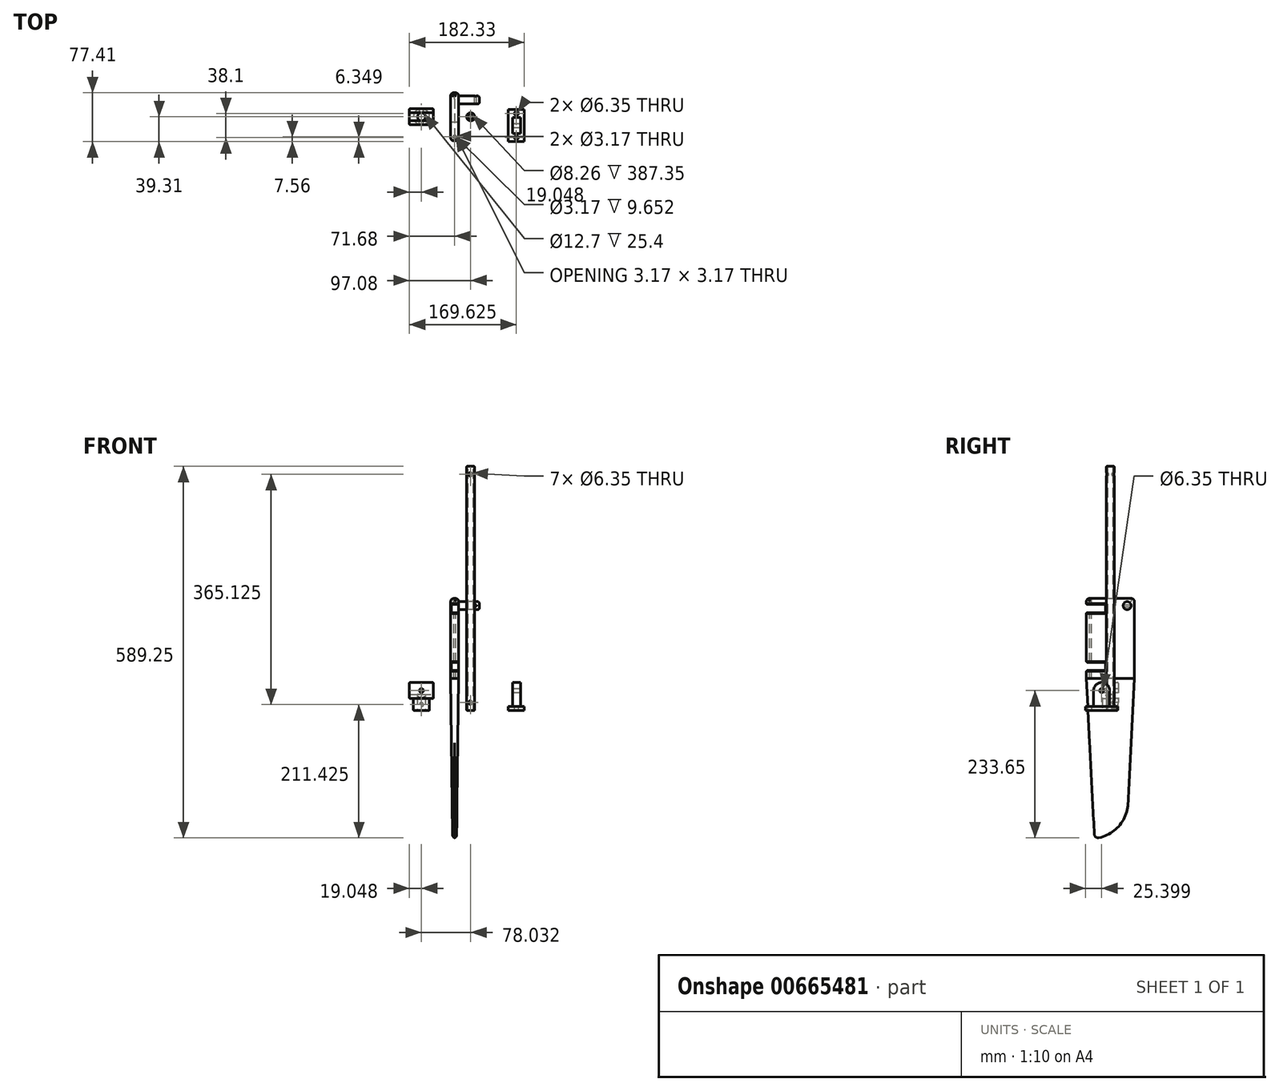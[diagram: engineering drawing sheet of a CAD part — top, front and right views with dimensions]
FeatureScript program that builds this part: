
annotation { "Feature Type Name" : "Feature", "Feature Type Description" : "" }
export const myFeature = defineFeature(function(context is Context, id is Id, definition is map)
    precondition{}
    {
        {
            var Q0;
            Q0=qCreatedBy(makeId("Right.planeOp"),FACE);
            var sketch = newSketch(context, id + "F0", { "sketchPlane" : qUnion([Q0])});
            skLineSegment(sketch, "E0", {"start": v(-41.4, 49.75) * mm, "end": v(34.8, 49.75) * mm});
            skLineSegment(sketch, "E1", {"start": v(34.8, 49.75) * mm, "end": v(34.8, -205.02) * mm});
            skArc(sketch, "E2", {"start": v(-20.7, -187.52) * mm, "mid": v(-12.8, -199.16) * mm, "end": v(0, -205.02) * mm});
            skLineSegment(sketch, "E3", {"start": v(-41.4, 49.75) * mm, "end": v(-20.7, -187.52) * mm});
            skLineSegment(sketch, "E4", {"start": v(0, -205.02) * mm, "end": v(34.8, -205.02) * mm});
            skSolve(sketch);
        }
        {
            var Q0;
            Q0=qCreatedBy(makeId("Top.planeOp"),FACE);
            cPlane(context, id + "F1", {"entities" : qUnion([Q0]), "cplaneType" : CPlaneType.OFFSET, "offset" : 50.8 * mm, "width" : 152.4 * mm, "height" : 152.4 * mm});
        }
        {
            var Q0;
            Q0=qCreatedBy(makeId("Top.planeOp"),FACE);
            cPlane(context, id + "F2", {"entities" : qUnion([Q0]), "cplaneType" : CPlaneType.OFFSET, "offset" : 203.2 * mm, "oppositeDirection" : true, "width" : 152.4 * mm, "height" : 152.4 * mm});
        }
        {
            var Q0;
            Q0=qCreatedBy(id+"F2.planeOp",FACE);
            var sketch = newSketch(context, id + "F3", { "sketchPlane" : qUnion([Q0])});
            skLineSegment(sketch, "E5.bottom", {"start": v(-3.18, 25.4) * mm, "end": v(3.17, 25.4) * mm});
            skLineSegment(sketch, "E5.top", {"start": v(-3.17, -25.4) * mm, "end": v(3.18, -25.4) * mm});
            skLineSegment(sketch, "E5.left", {"start": v(-3.18, 25.4) * mm, "end": v(-3.17, -25.4) * mm});
            skLineSegment(sketch, "E5.right", {"start": v(3.17, 25.4) * mm, "end": v(3.18, -25.4) * mm});
            skPoint(sketch, "E5.middle", {"position": v(0, 0) * mm});
            skSolve(sketch);
        }
        {
            var Q0;
            Q0=qCreatedBy(id+"F1.planeOp",FACE);
            var sketch = newSketch(context, id + "F4", { "sketchPlane" : qUnion([Q0])});
            skLineSegment(sketch, "E6.bottom", {"start": v(-6.35, 38.1) * mm, "end": v(6.35, 38.1) * mm});
            skLineSegment(sketch, "E6.top", {"start": v(-6.35, -38.1) * mm, "end": v(6.35, -38.1) * mm});
            skLineSegment(sketch, "E6.left", {"start": v(-6.35, 38.1) * mm, "end": v(-6.35, -38.1) * mm});
            skLineSegment(sketch, "E6.right", {"start": v(6.35, 38.1) * mm, "end": v(6.35, -38.1) * mm});
            skPoint(sketch, "E6.middle", {"position": v(0, 0) * mm});
            skSolve(sketch);
        }
        {
            var Q0;
            Q0=makeQuery(id+"F3.imprint","IMPRINT",FACE,{"disambiguationData":[TD([[makeQuery(id+"F3.imprint","IMPRINT",EDGE,{"derivedFrom":sQuery(id+"F3.wireOp",EDGE,"E5.bottom")}),-1.0]])]});
            var Q1;
            Q1=makeQuery(id+"F4.imprint","IMPRINT",FACE,{"disambiguationData":[TD([[makeQuery(id+"F4.imprint","IMPRINT",EDGE,{"derivedFrom":sQuery(id+"F4.wireOp",EDGE,"E6.bottom")}),-1.0]])]});
            loft(context, id + "F5", {"sheetProfilesArray" : [{ "sheetProfileEntities" : qUnion([Q0]) }, { "sheetProfileEntities" : qUnion([Q1]) }]});
        }
        {
            var Q0;
            Q0=makeQuery(id+"F5.opLoft","MID_CAP_EDGE",EDGE,{"disambiguationData":[OSD([sQuery(id+"F3.wireOp",EDGE,"E5.bottom"),sQuery(id+"F3.wireOp",EDGE,"E5.left"),sQuery(id+"F3.wireOp",EDGE,"E5.right")])],"capPos":0.0});
            fillet(context, id + "F6", {"entities" : qUnion([Q0]), "radius" : 58.8 * mm, "tangentPropagation" : true, "allowEdgeOverflow" : false});
        }
        {
            var Q0;
            {var subQ0=sQuery(id+"F3.wireOp",EDGE,"E5.right");var subQ1=sQuery(id+"F3.wireOp",EDGE,"E5.left");Q0=makeQuery(id+"F6.opFillet","BLEND_EDGE",EDGE,{"blendedFrom":[makeQuery(id+"F5.opLoft","MID_CAP_EDGE",EDGE,{"disambiguationData":[OSD([sQuery(id+"F3.wireOp",EDGE,"E5.bottom"),subQ1,subQ0])],"capPos":0.0}),makeQuery(id+"F5.opLoft","SWEPT_FACE",FACE,{"disambiguationData":[OSD([sQuery(id+"F3.wireOp",EDGE,"E5.top"),subQ1,subQ0,sQuery(id+"F4.wireOp",EDGE,"E6.top"),sQuery(id+"F4.wireOp",EDGE,"E6.left"),sQuery(id+"F4.wireOp",EDGE,"E6.right")])]})],"blendedInto":[makeQuery(id+"F5.opLoft","SWEPT_FACE",FACE,{"disambiguationData":[OSD([sQuery(id+"F3.wireOp",EDGE,"E5.top"),subQ1,subQ0,sQuery(id+"F4.wireOp",EDGE,"E6.top"),sQuery(id+"F4.wireOp",EDGE,"E6.left"),sQuery(id+"F4.wireOp",EDGE,"E6.right")])]})]});}
            fillet(context, id + "F7", {"entities" : qUnion([Q0]), "radius" : 6.33 * mm, "tangentPropagation" : true, "allowEdgeOverflow" : false});
        }
        {
            var Q0;
            {var subQ0=sQuery(id+"F3.wireOp",EDGE,"E5.right");var subQ1=sQuery(id+"F3.wireOp",EDGE,"E5.bottom");Q0=makeQuery(id+"F6.opFillet","BLEND_EDGE",EDGE,{"blendedFrom":[makeQuery(id+"F5.opLoft","MID_CAP_EDGE",EDGE,{"disambiguationData":[OSD([subQ1,sQuery(id+"F3.wireOp",EDGE,"E5.left"),subQ0])],"capPos":0.0}),makeQuery(id+"F5.opLoft","SWEPT_FACE",FACE,{"disambiguationData":[OSD([subQ1,sQuery(id+"F3.wireOp",EDGE,"E5.top"),subQ0,sQuery(id+"F4.wireOp",EDGE,"E6.bottom"),sQuery(id+"F4.wireOp",EDGE,"E6.top"),sQuery(id+"F4.wireOp",EDGE,"E6.right")])]})],"blendedInto":[makeQuery(id+"F5.opLoft","SWEPT_FACE",FACE,{"disambiguationData":[OSD([subQ1,sQuery(id+"F3.wireOp",EDGE,"E5.top"),subQ0,sQuery(id+"F4.wireOp",EDGE,"E6.bottom"),sQuery(id+"F4.wireOp",EDGE,"E6.top"),sQuery(id+"F4.wireOp",EDGE,"E6.right")])]})]});}
            var Q1;
            {var subQ0=sQuery(id+"F3.wireOp",EDGE,"E5.left");var subQ1=sQuery(id+"F3.wireOp",EDGE,"E5.bottom");Q1=makeQuery(id+"F6.opFillet","BLEND_EDGE",EDGE,{"blendedFrom":[makeQuery(id+"F5.opLoft","MID_CAP_EDGE",EDGE,{"disambiguationData":[OSD([subQ1,subQ0,sQuery(id+"F3.wireOp",EDGE,"E5.right")])],"capPos":0.0}),makeQuery(id+"F5.opLoft","SWEPT_FACE",FACE,{"disambiguationData":[OSD([subQ1,sQuery(id+"F3.wireOp",EDGE,"E5.top"),subQ0,sQuery(id+"F4.wireOp",EDGE,"E6.bottom"),sQuery(id+"F4.wireOp",EDGE,"E6.top"),sQuery(id+"F4.wireOp",EDGE,"E6.left")])]})],"blendedInto":[makeQuery(id+"F5.opLoft","SWEPT_FACE",FACE,{"disambiguationData":[OSD([subQ1,sQuery(id+"F3.wireOp",EDGE,"E5.top"),subQ0,sQuery(id+"F4.wireOp",EDGE,"E6.bottom"),sQuery(id+"F4.wireOp",EDGE,"E6.top"),sQuery(id+"F4.wireOp",EDGE,"E6.left")])]})]});}
            fillet(context, id + "F8", {"entities" : qUnion([Q0, Q1]), "radius" : 5.08 * mm, "tangentPropagation" : true, "allowEdgeOverflow" : false});
        }
        {
            var Q0;
            Q0=makeQuery(id+"F5.opLoft","CAP_FACE",FACE,{"disambiguationData":[OSD([makeQuery(id+"F4.imprint","IMPRINT",FACE,{"disambiguationData":[TD([[makeQuery(id+"F4.imprint","IMPRINT",EDGE,{"derivedFrom":sQuery(id+"F4.wireOp",EDGE,"E6.bottom")}),-1.0]])]})])],"isStart":true});
            extrude(context, id + "F9", {"entities" : qUnion([Q0]), "depth" : 127 * mm, "offsetDistance" : 25.4 * mm});
        }
        {
            var Q0;
            Q0=makeQuery(id+"F9.opExtrude","SWEPT_FACE",FACE,{"disambiguationData":[OSD([sQuery(id+"F4.wireOp",EDGE,"E6.bottom"),sQuery(id+"F4.wireOp",EDGE,"E6.top"),sQuery(id+"F4.wireOp",EDGE,"E6.right")])]});
            var sketch = newSketch(context, id + "F10", { "sketchPlane" : qUnion([Q0])});
            skLineSegment(sketch, "E7.bottom", {"start": v(-58.18, 168.15) * mm, "end": v(-7.85, 168.15) * mm});
            skLineSegment(sketch, "E7.top", {"start": v(-58.18, 155.2) * mm, "end": v(-7.85, 155.2) * mm});
            skLineSegment(sketch, "E7.left", {"start": v(-58.18, 168.15) * mm, "end": v(-58.18, 155.2) * mm});
            skLineSegment(sketch, "E7.right", {"start": v(-7.85, 168.15) * mm, "end": v(-7.85, 155.2) * mm});
            skPoint(sketch, "E7.middle", {"position": v(-33.02, 161.67) * mm});
            skLineSegment(sketch, "E8.bottom", {"start": v(-58.18, 76.45) * mm, "end": v(-7.85, 76.45) * mm});
            skLineSegment(sketch, "E8.top", {"start": v(-58.18, 63.5) * mm, "end": v(-7.85, 63.5) * mm});
            skLineSegment(sketch, "E8.left", {"start": v(-58.18, 76.45) * mm, "end": v(-58.18, 63.5) * mm});
            skLineSegment(sketch, "E8.right", {"start": v(-7.85, 76.45) * mm, "end": v(-7.85, 63.5) * mm});
            skPoint(sketch, "E8.middle", {"position": v(-33.02, 69.98) * mm});
            skSolve(sketch);
        }
        {
            var Q0;
            {var subQ0=sQuery(id+"F10.wireOp",EDGE,"E7.right");Q0=makeQuery(id+"F10.imprint","IMPRINT",FACE,{"disambiguationData":[TD([[makeQuery(id+"F10.imprint","IMPRINT",EDGE,{"derivedFrom":subQ0}),-1.0]])]});}
            var Q1;
            {var subQ0=sQuery(id+"F10.wireOp",EDGE,"E7.left");Q1=makeQuery(id+"F10.imprint","IMPRINT",FACE,{"disambiguationData":[TD([[makeQuery(id+"F10.imprint","IMPRINT",EDGE,{"derivedFrom":subQ0}),1.0]])]});}
            var Q2;
            {var subQ0=sQuery(id+"F10.wireOp",EDGE,"E8.right");Q2=makeQuery(id+"F10.imprint","IMPRINT",FACE,{"disambiguationData":[TD([[makeQuery(id+"F10.imprint","IMPRINT",EDGE,{"derivedFrom":subQ0}),-1.0]])]});}
            var Q3;
            {var subQ0=sQuery(id+"F10.wireOp",EDGE,"E8.left");Q3=makeQuery(id+"F10.imprint","IMPRINT",FACE,{"disambiguationData":[TD([[makeQuery(id+"F10.imprint","IMPRINT",EDGE,{"derivedFrom":subQ0}),1.0]])]});}
            extrude(context, id + "F11", {"entities" : qUnion([Q0, Q1, Q2, Q3]), "operationType" : NewBodyOperationType.REMOVE, "oppositeDirection" : true, "depth" : 25.4 * mm, "offsetDistance" : 25.4 * mm});
        }
        {
            var Q0;
            Q0=makeQuery(id+"F11.boolean.opBoolean","COPY",EDGE,{"derivedFrom":makeQuery(id+"F11.opExtrude","CAP_EDGE",EDGE,{"disambiguationData":[OSD([sQuery(id+"F10.wireOp",EDGE,"E7.bottom")])],"isStart":true})});
            var Q1;
            Q1=makeQuery(id+"F11.boolean.opBoolean","INTERSECT",EDGE,{"derivedFrom":[makeQuery(id+"F9.opExtrude","SWEPT_FACE",FACE,{"disambiguationData":[OSD([sQuery(id+"F4.wireOp",EDGE,"E6.bottom"),sQuery(id+"F4.wireOp",EDGE,"E6.top"),sQuery(id+"F4.wireOp",EDGE,"E6.left")])]}),makeQuery(id+"F11.opExtrude","SWEPT_FACE",FACE,{"disambiguationData":[OSD([sQuery(id+"F10.wireOp",EDGE,"E7.top")])]})]});
            var Q2;
            {var subQ0=sQuery(id+"F4.wireOp",EDGE,"E6.top");var subQ1=sQuery(id+"F4.wireOp",EDGE,"E6.left");Q2=makeQuery(id+"F11.boolean.opBoolean","INTERSECT",EDGE,{"derivedFrom":[makeQuery(id+"F9.opExtrude","SWEPT_FACE",FACE,{"disambiguationData":[OSD([sQuery(id+"F3.wireOp",EDGE,"E5.top"),sQuery(id+"F3.wireOp",EDGE,"E5.left"),subQ0,subQ1,makeQuery(id+"F4.imprint","IMPRINT",FACE,{"disambiguationData":[TD([[makeQuery(id+"F4.imprint","IMPRINT",EDGE,{"derivedFrom":sQuery(id+"F4.wireOp",EDGE,"E6.bottom")}),-1.0]])]})])]}),makeQuery(id+"F11.opExtrude","SWEPT_FACE",FACE,{"disambiguationData":[OSD([sQuery(id+"F10.wireOp",EDGE,"E7.top")])]})]});}
            var Q3;
            {var subQ0=sQuery(id+"F4.wireOp",EDGE,"E6.top");var subQ1=sQuery(id+"F4.wireOp",EDGE,"E6.right");Q3=makeQuery(id+"F11.boolean.opBoolean","INTERSECT",EDGE,{"derivedFrom":[makeQuery(id+"F9.opExtrude","SWEPT_FACE",FACE,{"disambiguationData":[OSD([sQuery(id+"F3.wireOp",EDGE,"E5.top"),sQuery(id+"F3.wireOp",EDGE,"E5.right"),subQ0,subQ1,makeQuery(id+"F4.imprint","IMPRINT",FACE,{"disambiguationData":[TD([[makeQuery(id+"F4.imprint","IMPRINT",EDGE,{"derivedFrom":sQuery(id+"F4.wireOp",EDGE,"E6.bottom")}),-1.0]])]})])]}),makeQuery(id+"F11.opExtrude","SWEPT_FACE",FACE,{"disambiguationData":[OSD([sQuery(id+"F10.wireOp",EDGE,"E7.top")])]})]});}
            var Q4;
            Q4=makeQuery(id+"F11.boolean.opBoolean","COPY",EDGE,{"derivedFrom":makeQuery(id+"F11.opExtrude","CAP_EDGE",EDGE,{"disambiguationData":[OSD([sQuery(id+"F10.wireOp",EDGE,"E7.top")])],"isStart":true})});
            var Q5;
            Q5=makeQuery(id+"F11.boolean.opBoolean","INTERSECT",EDGE,{"derivedFrom":[makeQuery(id+"F9.opExtrude","SWEPT_FACE",FACE,{"disambiguationData":[OSD([sQuery(id+"F4.wireOp",EDGE,"E6.top"),sQuery(id+"F4.wireOp",EDGE,"E6.left"),sQuery(id+"F4.wireOp",EDGE,"E6.right")])]}),makeQuery(id+"F11.opExtrude","SWEPT_FACE",FACE,{"disambiguationData":[OSD([sQuery(id+"F10.wireOp",EDGE,"E7.top")])]})]});
            var Q6;
            {var subQ0=sQuery(id+"F4.wireOp",EDGE,"E6.top");var subQ1=sQuery(id+"F4.wireOp",EDGE,"E6.right");Q6=makeQuery(id+"F11.boolean.opBoolean","INTERSECT",EDGE,{"derivedFrom":[makeQuery(id+"F9.opExtrude","SWEPT_FACE",FACE,{"disambiguationData":[OSD([sQuery(id+"F3.wireOp",EDGE,"E5.top"),sQuery(id+"F3.wireOp",EDGE,"E5.right"),subQ0,subQ1,makeQuery(id+"F4.imprint","IMPRINT",FACE,{"disambiguationData":[TD([[makeQuery(id+"F4.imprint","IMPRINT",EDGE,{"derivedFrom":sQuery(id+"F4.wireOp",EDGE,"E6.bottom")}),-1.0]])]})])]}),makeQuery(id+"F11.opExtrude","SWEPT_FACE",FACE,{"disambiguationData":[OSD([sQuery(id+"F10.wireOp",EDGE,"E7.bottom")])]})]});}
            var Q7;
            Q7=makeQuery(id+"F11.boolean.opBoolean","INTERSECT",EDGE,{"derivedFrom":[makeQuery(id+"F9.opExtrude","SWEPT_FACE",FACE,{"disambiguationData":[OSD([sQuery(id+"F4.wireOp",EDGE,"E6.top"),sQuery(id+"F4.wireOp",EDGE,"E6.left"),sQuery(id+"F4.wireOp",EDGE,"E6.right")])]}),makeQuery(id+"F11.opExtrude","SWEPT_FACE",FACE,{"disambiguationData":[OSD([sQuery(id+"F10.wireOp",EDGE,"E7.bottom")])]})]});
            var Q8;
            {var subQ0=sQuery(id+"F4.wireOp",EDGE,"E6.top");var subQ1=sQuery(id+"F4.wireOp",EDGE,"E6.left");Q8=makeQuery(id+"F11.boolean.opBoolean","INTERSECT",EDGE,{"derivedFrom":[makeQuery(id+"F9.opExtrude","SWEPT_FACE",FACE,{"disambiguationData":[OSD([sQuery(id+"F3.wireOp",EDGE,"E5.top"),sQuery(id+"F3.wireOp",EDGE,"E5.left"),subQ0,subQ1,makeQuery(id+"F4.imprint","IMPRINT",FACE,{"disambiguationData":[TD([[makeQuery(id+"F4.imprint","IMPRINT",EDGE,{"derivedFrom":sQuery(id+"F4.wireOp",EDGE,"E6.bottom")}),-1.0]])]})])]}),makeQuery(id+"F11.opExtrude","SWEPT_FACE",FACE,{"disambiguationData":[OSD([sQuery(id+"F10.wireOp",EDGE,"E7.bottom")])]})]});}
            var Q9;
            Q9=makeQuery(id+"F11.boolean.opBoolean","INTERSECT",EDGE,{"derivedFrom":[makeQuery(id+"F9.opExtrude","SWEPT_FACE",FACE,{"disambiguationData":[OSD([sQuery(id+"F4.wireOp",EDGE,"E6.bottom"),sQuery(id+"F4.wireOp",EDGE,"E6.top"),sQuery(id+"F4.wireOp",EDGE,"E6.left")])]}),makeQuery(id+"F11.opExtrude","SWEPT_FACE",FACE,{"disambiguationData":[OSD([sQuery(id+"F10.wireOp",EDGE,"E7.bottom")])]})]});
            var Q10;
            Q10=makeQuery(id+"F11.boolean.opBoolean","INTERSECT",EDGE,{"derivedFrom":[makeQuery(id+"F9.opExtrude","SWEPT_FACE",FACE,{"disambiguationData":[OSD([sQuery(id+"F4.wireOp",EDGE,"E6.bottom"),sQuery(id+"F4.wireOp",EDGE,"E6.top"),sQuery(id+"F4.wireOp",EDGE,"E6.left")])]}),makeQuery(id+"F11.opExtrude","SWEPT_FACE",FACE,{"disambiguationData":[OSD([sQuery(id+"F10.wireOp",EDGE,"E7.right")])]})]});
            var Q11;
            Q11=makeQuery(id+"F11.boolean.opBoolean","COPY",EDGE,{"derivedFrom":makeQuery(id+"F11.opExtrude","CAP_EDGE",EDGE,{"disambiguationData":[OSD([sQuery(id+"F10.wireOp",EDGE,"E7.right")])],"isStart":true})});
            var Q12;
            Q12=makeQuery(id+"F11.boolean.opBoolean","INTERSECT",EDGE,{"derivedFrom":[makeQuery(id+"F9.opExtrude","SWEPT_FACE",FACE,{"disambiguationData":[OSD([sQuery(id+"F4.wireOp",EDGE,"E6.bottom"),sQuery(id+"F4.wireOp",EDGE,"E6.top"),sQuery(id+"F4.wireOp",EDGE,"E6.left")])]}),makeQuery(id+"F11.opExtrude","SWEPT_FACE",FACE,{"disambiguationData":[OSD([sQuery(id+"F10.wireOp",EDGE,"E8.right")])]})]});
            var Q13;
            Q13=makeQuery(id+"F11.boolean.opBoolean","INTERSECT",EDGE,{"derivedFrom":[makeQuery(id+"F9.opExtrude","SWEPT_FACE",FACE,{"disambiguationData":[OSD([sQuery(id+"F4.wireOp",EDGE,"E6.bottom"),sQuery(id+"F4.wireOp",EDGE,"E6.top"),sQuery(id+"F4.wireOp",EDGE,"E6.left")])]}),makeQuery(id+"F11.opExtrude","SWEPT_FACE",FACE,{"disambiguationData":[OSD([sQuery(id+"F10.wireOp",EDGE,"E8.top")])]})]});
            var Q14;
            Q14=makeQuery(id+"F11.boolean.opBoolean","INTERSECT",EDGE,{"derivedFrom":[makeQuery(id+"F9.opExtrude","SWEPT_FACE",FACE,{"disambiguationData":[OSD([sQuery(id+"F4.wireOp",EDGE,"E6.bottom"),sQuery(id+"F4.wireOp",EDGE,"E6.top"),sQuery(id+"F4.wireOp",EDGE,"E6.left")])]}),makeQuery(id+"F11.opExtrude","SWEPT_FACE",FACE,{"disambiguationData":[OSD([sQuery(id+"F10.wireOp",EDGE,"E8.bottom")])]})]});
            var Q15;
            Q15=makeQuery(id+"F11.boolean.opBoolean","COPY",EDGE,{"derivedFrom":makeQuery(id+"F11.opExtrude","CAP_EDGE",EDGE,{"disambiguationData":[OSD([sQuery(id+"F10.wireOp",EDGE,"E8.right")])],"isStart":true})});
            var Q16;
            Q16=makeQuery(id+"F11.boolean.opBoolean","COPY",EDGE,{"derivedFrom":makeQuery(id+"F11.opExtrude","CAP_EDGE",EDGE,{"disambiguationData":[OSD([sQuery(id+"F10.wireOp",EDGE,"E8.top")])],"isStart":true})});
            var Q17;
            {var subQ0=sQuery(id+"F4.wireOp",EDGE,"E6.top");var subQ1=sQuery(id+"F4.wireOp",EDGE,"E6.left");Q17=makeQuery(id+"F11.boolean.opBoolean","INTERSECT",EDGE,{"derivedFrom":[makeQuery(id+"F9.opExtrude","SWEPT_FACE",FACE,{"disambiguationData":[OSD([sQuery(id+"F3.wireOp",EDGE,"E5.top"),sQuery(id+"F3.wireOp",EDGE,"E5.left"),subQ0,subQ1,makeQuery(id+"F4.imprint","IMPRINT",FACE,{"disambiguationData":[TD([[makeQuery(id+"F4.imprint","IMPRINT",EDGE,{"derivedFrom":sQuery(id+"F4.wireOp",EDGE,"E6.bottom")}),-1.0]])]})])]}),makeQuery(id+"F11.opExtrude","SWEPT_FACE",FACE,{"disambiguationData":[OSD([sQuery(id+"F10.wireOp",EDGE,"E8.top")])]})]});}
            var Q18;
            {var subQ0=sQuery(id+"F4.wireOp",EDGE,"E6.top");var subQ1=sQuery(id+"F4.wireOp",EDGE,"E6.right");Q18=makeQuery(id+"F11.boolean.opBoolean","INTERSECT",EDGE,{"derivedFrom":[makeQuery(id+"F9.opExtrude","SWEPT_FACE",FACE,{"disambiguationData":[OSD([sQuery(id+"F3.wireOp",EDGE,"E5.top"),sQuery(id+"F3.wireOp",EDGE,"E5.right"),subQ0,subQ1,makeQuery(id+"F4.imprint","IMPRINT",FACE,{"disambiguationData":[TD([[makeQuery(id+"F4.imprint","IMPRINT",EDGE,{"derivedFrom":sQuery(id+"F4.wireOp",EDGE,"E6.bottom")}),-1.0]])]})])]}),makeQuery(id+"F11.opExtrude","SWEPT_FACE",FACE,{"disambiguationData":[OSD([sQuery(id+"F10.wireOp",EDGE,"E8.top")])]})]});}
            var Q19;
            Q19=makeQuery(id+"F11.boolean.opBoolean","INTERSECT",EDGE,{"derivedFrom":[makeQuery(id+"F9.opExtrude","SWEPT_FACE",FACE,{"disambiguationData":[OSD([sQuery(id+"F4.wireOp",EDGE,"E6.top"),sQuery(id+"F4.wireOp",EDGE,"E6.left"),sQuery(id+"F4.wireOp",EDGE,"E6.right")])]}),makeQuery(id+"F11.opExtrude","SWEPT_FACE",FACE,{"disambiguationData":[OSD([sQuery(id+"F10.wireOp",EDGE,"E8.top")])]})]});
            var Q20;
            {var subQ0=sQuery(id+"F4.wireOp",EDGE,"E6.top");var subQ1=sQuery(id+"F4.wireOp",EDGE,"E6.left");Q20=makeQuery(id+"F11.boolean.opBoolean","INTERSECT",EDGE,{"derivedFrom":[makeQuery(id+"F9.opExtrude","SWEPT_FACE",FACE,{"disambiguationData":[OSD([sQuery(id+"F3.wireOp",EDGE,"E5.top"),sQuery(id+"F3.wireOp",EDGE,"E5.left"),subQ0,subQ1,makeQuery(id+"F4.imprint","IMPRINT",FACE,{"disambiguationData":[TD([[makeQuery(id+"F4.imprint","IMPRINT",EDGE,{"derivedFrom":sQuery(id+"F4.wireOp",EDGE,"E6.bottom")}),-1.0]])]})])]}),makeQuery(id+"F11.opExtrude","SWEPT_FACE",FACE,{"disambiguationData":[OSD([sQuery(id+"F10.wireOp",EDGE,"E8.bottom")])]})]});}
            var Q21;
            Q21=makeQuery(id+"F11.boolean.opBoolean","INTERSECT",EDGE,{"derivedFrom":[makeQuery(id+"F9.opExtrude","SWEPT_FACE",FACE,{"disambiguationData":[OSD([sQuery(id+"F4.wireOp",EDGE,"E6.top"),sQuery(id+"F4.wireOp",EDGE,"E6.left"),sQuery(id+"F4.wireOp",EDGE,"E6.right")])]}),makeQuery(id+"F11.opExtrude","SWEPT_FACE",FACE,{"disambiguationData":[OSD([sQuery(id+"F10.wireOp",EDGE,"E8.bottom")])]})]});
            var Q22;
            {var subQ0=sQuery(id+"F4.wireOp",EDGE,"E6.top");var subQ1=sQuery(id+"F4.wireOp",EDGE,"E6.right");Q22=makeQuery(id+"F11.boolean.opBoolean","INTERSECT",EDGE,{"derivedFrom":[makeQuery(id+"F9.opExtrude","SWEPT_FACE",FACE,{"disambiguationData":[OSD([sQuery(id+"F3.wireOp",EDGE,"E5.top"),sQuery(id+"F3.wireOp",EDGE,"E5.right"),subQ0,subQ1,makeQuery(id+"F4.imprint","IMPRINT",FACE,{"disambiguationData":[TD([[makeQuery(id+"F4.imprint","IMPRINT",EDGE,{"derivedFrom":sQuery(id+"F4.wireOp",EDGE,"E6.bottom")}),-1.0]])]})])]}),makeQuery(id+"F11.opExtrude","SWEPT_FACE",FACE,{"disambiguationData":[OSD([sQuery(id+"F10.wireOp",EDGE,"E8.bottom")])]})]});}
            var Q23;
            Q23=makeQuery(id+"F11.boolean.opBoolean","COPY",EDGE,{"derivedFrom":makeQuery(id+"F11.opExtrude","CAP_EDGE",EDGE,{"disambiguationData":[OSD([sQuery(id+"F10.wireOp",EDGE,"E8.bottom")])],"isStart":true})});
            chamfer(context, id + "F12", {"entities" : qUnion([Q0, Q1, Q2, Q3, Q4, Q5, Q6, Q7, Q8, Q9, Q10, Q11, Q12, Q13, Q14, Q15, Q16, Q17, Q18, Q19, Q20, Q21, Q22, Q23]), "width" : 1.27 * mm, "tangentPropagation" : true});
        }
        {
            var Q0;
            Q0=makeQuery(id+"F9.opExtrude","CAP_FACE",FACE,{"disambiguationData":[OSD([makeQuery(id+"F4.imprint","IMPRINT",FACE,{"disambiguationData":[TD([[makeQuery(id+"F4.imprint","IMPRINT",EDGE,{"derivedFrom":sQuery(id+"F4.wireOp",EDGE,"E6.bottom")}),-1.0]])]})])],"isStart":false});
            var sketch = newSketch(context, id + "F13", { "sketchPlane" : qUnion([Q0])});
            skCircle(sketch, "E9", {"center": v(0, -31.75) * mm, "radius": 1.59 * mm});
            skSolve(sketch);
        }
        {
            var Q0;
            Q0=makeQuery(id+"F13.imprint","IMPRINT",FACE,{"disambiguationData":[TD([[makeQuery(id+"F13.imprint","IMPRINT",EDGE,{"derivedFrom":sQuery(id+"F13.wireOp",EDGE,"E9")}),1.0]])]});
            extrude(context, id + "F14", {"entities" : qUnion([Q0]), "operationType" : NewBodyOperationType.REMOVE, "oppositeDirection" : true, "depth" : 127 * mm, "offsetDistance" : 25.4 * mm});
        }
        {
            var Q0;
            Q0=makeQuery(id+"F9.opExtrude","CAP_EDGE",EDGE,{"disambiguationData":[OSD([sQuery(id+"F4.wireOp",EDGE,"E6.bottom"),sQuery(id+"F4.wireOp",EDGE,"E6.top"),sQuery(id+"F4.wireOp",EDGE,"E6.left")])],"isStart":false});
            var Q1;
            Q1=makeQuery(id+"F9.opExtrude","CAP_EDGE",EDGE,{"disambiguationData":[OSD([sQuery(id+"F4.wireOp",EDGE,"E6.bottom"),sQuery(id+"F4.wireOp",EDGE,"E6.top"),sQuery(id+"F4.wireOp",EDGE,"E6.right")])],"isStart":false});
            var Q2;
            {var subQ0=sQuery(id+"F4.wireOp",EDGE,"E6.top");var subQ1=sQuery(id+"F4.wireOp",EDGE,"E6.right");Q2=makeQuery(id+"F9.opExtrude","CAP_EDGE",EDGE,{"disambiguationData":[OSD([sQuery(id+"F3.wireOp",EDGE,"E5.top"),sQuery(id+"F3.wireOp",EDGE,"E5.right"),subQ0,subQ1,makeQuery(id+"F4.imprint","IMPRINT",FACE,{"disambiguationData":[TD([[makeQuery(id+"F4.imprint","IMPRINT",EDGE,{"derivedFrom":sQuery(id+"F4.wireOp",EDGE,"E6.bottom")}),-1.0]])]})])],"isStart":false});}
            var Q3;
            {var subQ0=sQuery(id+"F4.wireOp",EDGE,"E6.top");var subQ1=sQuery(id+"F4.wireOp",EDGE,"E6.left");Q3=makeQuery(id+"F9.opExtrude","CAP_EDGE",EDGE,{"disambiguationData":[OSD([sQuery(id+"F3.wireOp",EDGE,"E5.top"),sQuery(id+"F3.wireOp",EDGE,"E5.left"),subQ0,subQ1,makeQuery(id+"F4.imprint","IMPRINT",FACE,{"disambiguationData":[TD([[makeQuery(id+"F4.imprint","IMPRINT",EDGE,{"derivedFrom":sQuery(id+"F4.wireOp",EDGE,"E6.bottom")}),-1.0]])]})])],"isStart":false});}
            var Q4;
            Q4=makeQuery(id+"F9.opExtrude","CAP_EDGE",EDGE,{"disambiguationData":[OSD([sQuery(id+"F4.wireOp",EDGE,"E6.top"),sQuery(id+"F4.wireOp",EDGE,"E6.left"),sQuery(id+"F4.wireOp",EDGE,"E6.right")])],"isStart":false});
            var Q5;
            {var subQ0=sQuery(id+"F4.wireOp",EDGE,"E6.bottom");var subQ1=sQuery(id+"F4.wireOp",EDGE,"E6.left");Q5=makeQuery(id+"F9.opExtrude","CAP_EDGE",EDGE,{"disambiguationData":[OSD([sQuery(id+"F3.wireOp",EDGE,"E5.bottom"),sQuery(id+"F3.wireOp",EDGE,"E5.left"),subQ0,subQ1,makeQuery(id+"F4.imprint","IMPRINT",FACE,{"disambiguationData":[TD([[makeQuery(id+"F4.imprint","IMPRINT",EDGE,{"derivedFrom":subQ0}),-1.0]])]})])],"isStart":false});}
            var Q6;
            {var subQ0=sQuery(id+"F4.wireOp",EDGE,"E6.bottom");var subQ1=sQuery(id+"F4.wireOp",EDGE,"E6.right");Q6=makeQuery(id+"F9.opExtrude","CAP_EDGE",EDGE,{"disambiguationData":[OSD([sQuery(id+"F3.wireOp",EDGE,"E5.bottom"),sQuery(id+"F3.wireOp",EDGE,"E5.right"),subQ0,subQ1,makeQuery(id+"F4.imprint","IMPRINT",FACE,{"disambiguationData":[TD([[makeQuery(id+"F4.imprint","IMPRINT",EDGE,{"derivedFrom":subQ0}),-1.0]])]})])],"isStart":false});}
            var Q7;
            Q7=makeQuery(id+"F9.opExtrude","CAP_EDGE",EDGE,{"disambiguationData":[OSD([sQuery(id+"F4.wireOp",EDGE,"E6.bottom"),sQuery(id+"F4.wireOp",EDGE,"E6.left"),sQuery(id+"F4.wireOp",EDGE,"E6.right")])],"isStart":false});
            fillet(context, id + "F15", {"entities" : qUnion([Q0, Q1, Q2, Q3, Q4, Q5, Q6, Q7]), "radius" : 5.08 * mm, "tangentPropagation" : true, "allowEdgeOverflow" : false});
        }
        {
            var Q0;
            Q0=qCreatedBy(makeId("Top.planeOp"),FACE);
            var sketch = newSketch(context, id + "F16", { "sketchPlane" : qUnion([Q0])});
            skCircle(sketch, "E10", {"center": v(25.4, 0) * mm, "radius": 6.35 * mm});
            skSolve(sketch);
        }
        {
            var Q0;
            Q0 = qSketchRegion(id + "F16", true);
            extrude(context, id + "F17", {"entities" : qUnion([Q0]), "depth" : 387.35 * mm, "offsetDistance" : 25.4 * mm});
        }
        {
            var Q0;
            Q0=qCreatedBy(makeId("Top.planeOp"),FACE);
            var sketch = newSketch(context, id + "F18", { "sketchPlane" : qUnion([Q0])});
            skCircle(sketch, "E11", {"center": v(-52.63, 0) * mm, "radius": 6.35 * mm});
            skCircle(sketch, "E12", {"center": v(-52.63, 0) * mm, "radius": 12.7 * mm});
            skSolve(sketch);
        }
        {
            var Q0;
            Q0=makeQuery(id+"F18.imprint","IMPRINT",FACE,{"disambiguationData":[TD([[makeQuery(id+"F18.imprint","IMPRINT",EDGE,{"derivedFrom":sQuery(id+"F18.wireOp",EDGE,"E11")}),-1.0]])]});
            extrude(context, id + "F19", {"entities" : qUnion([Q0]), "depth" : 19.05 * mm, "offsetDistance" : 25.4 * mm});
        }
        {
            var Q0;
            Q0=makeQuery(id+"F19.opExtrude","CAP_FACE",FACE,{"disambiguationData":[OSD([sQuery(id+"F18.wireOp",EDGE,"E11"),sQuery(id+"F18.wireOp",EDGE,"E12")])],"isStart":false});
            var sketch = newSketch(context, id + "F20", { "sketchPlane" : qUnion([Q0])});
            skLineSegment(sketch, "E13.bottom", {"start": v(-33.58, -12.7) * mm, "end": v(-71.68, -12.7) * mm});
            skLineSegment(sketch, "E13.top", {"start": v(-33.58, 12.7) * mm, "end": v(-71.68, 12.7) * mm});
            skLineSegment(sketch, "E13.left", {"start": v(-33.58, -12.7) * mm, "end": v(-33.58, 12.7) * mm});
            skLineSegment(sketch, "E13.right", {"start": v(-71.68, -12.7) * mm, "end": v(-71.68, 12.7) * mm});
            skPoint(sketch, "E13.middle", {"position": v(-52.63, 0) * mm});
            skLineSegment(sketch, "E14", {"start": v(-71.68, 6.35) * mm, "end": v(-33.58, 6.35) * mm});
            skLineSegment(sketch, "E15", {"start": v(-71.68, -6.35) * mm, "end": v(-33.58, -6.35) * mm});
            skSolve(sketch);
        }
        {
            var Q0;
            {var subQ4=sQuery(id+"F20.wireOp",EDGE,"E13.top");Q0=makeQuery(id+"F20.imprint","IMPRINT",FACE,{"disambiguationData":[TD([[makeQuery(id+"F20.imprint","IMPRINT",EDGE,{"derivedFrom":subQ4}),1.0]])]});}
            var Q1;
            {var subQ1=sQuery(id+"F20.wireOp",EDGE,"E13.bottom");Q1=makeQuery(id+"F20.imprint","IMPRINT",FACE,{"disambiguationData":[TD([[makeQuery(id+"F20.imprint","IMPRINT",EDGE,{"derivedFrom":subQ1}),-1.0]])]});}
            var Q2;
            {var subQ0=sQuery(id+"F20.wireOp",EDGE,"E15");var subQ1=makeQuery(id+"F19.opExtrude","CAP_EDGE",EDGE,{"disambiguationData":[OSD([sQuery(id+"F18.wireOp",EDGE,"E12")])],"isStart":false});var subQ2=makeQuery(id+"F20.imprint","INTERSECT",VERTEX,{"disambiguationData":[OD(0.0)],"derivedFrom":[subQ1,subQ0]});Q2=makeQuery(id+"F20.imprint","IMPRINT",FACE,{"disambiguationData":[TD([[makeQuery(id+"F20.imprint","IMPRINT",EDGE,{"disambiguationData":[TD([[subQ2,-1.0]])],"derivedFrom":subQ0}),-1.0]])]});}
            var Q3;
            {var subQ0=sQuery(id+"F20.wireOp",EDGE,"E14");var subQ1=makeQuery(id+"F19.opExtrude","CAP_EDGE",EDGE,{"disambiguationData":[OSD([sQuery(id+"F18.wireOp",EDGE,"E12")])],"isStart":false});var subQ2=makeQuery(id+"F20.imprint","INTERSECT",VERTEX,{"disambiguationData":[OD(0.0)],"derivedFrom":[subQ1,subQ0]});Q3=makeQuery(id+"F20.imprint","IMPRINT",FACE,{"disambiguationData":[TD([[makeQuery(id+"F20.imprint","IMPRINT",EDGE,{"disambiguationData":[TD([[subQ2,-1.0]])],"derivedFrom":subQ0}),1.0]])]});}
            extrude(context, id + "F21", {"entities" : qUnion([Q0, Q1, Q2, Q3]), "depth" : 25.4 * mm, "offsetDistance" : 25.4 * mm});
        }
        {
            var Q0;
            {var subQ0=sQuery(id+"F20.wireOp",EDGE,"E14");var subQ1=sQuery(id+"F20.wireOp",EDGE,"E13.right");var subQ2=makeQuery(id+"F20.imprint","INTERSECT",VERTEX,{"derivedFrom":[subQ1,subQ0]});Q0=makeQuery(id+"F20.imprint","IMPRINT",FACE,{"disambiguationData":[TD([[makeQuery(id+"F20.imprint","IMPRINT",EDGE,{"disambiguationData":[TD([[subQ2,1.0]])],"derivedFrom":subQ1}),-1.0]])]});}
            var Q1;
            {var subQ0=sQuery(id+"F20.wireOp",EDGE,"E14");var subQ1=sQuery(id+"F20.wireOp",EDGE,"E13.left");var subQ2=makeQuery(id+"F20.imprint","INTERSECT",VERTEX,{"derivedFrom":[subQ1,subQ0]});Q1=makeQuery(id+"F20.imprint","IMPRINT",FACE,{"disambiguationData":[TD([[makeQuery(id+"F20.imprint","IMPRINT",EDGE,{"disambiguationData":[TD([[subQ2,1.0]])],"derivedFrom":subQ1}),1.0]])]});}
            var Q2;
            {var subQ0=sQuery(id+"F20.wireOp",EDGE,"E14");var subQ1=makeQuery(id+"F19.opExtrude","CAP_EDGE",EDGE,{"disambiguationData":[OSD([sQuery(id+"F18.wireOp",EDGE,"E12")])],"isStart":false});var subQ2=makeQuery(id+"F20.imprint","INTERSECT",VERTEX,{"disambiguationData":[OD(0.0)],"derivedFrom":[subQ1,subQ0]});Q2=makeQuery(id+"F20.imprint","IMPRINT",FACE,{"disambiguationData":[TD([[makeQuery(id+"F20.imprint","IMPRINT",EDGE,{"disambiguationData":[TD([[subQ2,-1.0]])],"derivedFrom":subQ0}),-1.0]])]});}
            var Q3;
            {var subQ0=sQuery(id+"F20.wireOp",EDGE,"E14");var subQ1=makeQuery(id+"F19.opExtrude","CAP_EDGE",EDGE,{"disambiguationData":[OSD([sQuery(id+"F18.wireOp",EDGE,"E11")])],"isStart":false});var subQ2=makeQuery(id+"F20.imprint","INTERSECT",VERTEX,{"derivedFrom":[subQ1,subQ0]});Q3=makeQuery(id+"F20.imprint","IMPRINT",FACE,{"disambiguationData":[TD([[makeQuery(id+"F20.imprint","IMPRINT",EDGE,{"disambiguationData":[TD([[subQ2,-1.0]])],"derivedFrom":subQ0}),-1.0]])]});}
            extrude(context, id + "F22", {"entities" : qUnion([Q0, Q1, Q2, Q3]), "depth" : 6.35 * mm, "offsetDistance" : 25.4 * mm});
        }
        {
            var Q0;
            Q0=makeQuery(id+"F20.imprint","IMPRINT",FACE,{"disambiguationData":[TD([[makeQuery(id+"F20.imprint","IMPRINT",EDGE,{"derivedFrom":makeQuery(id+"F19.opExtrude","CAP_EDGE",EDGE,{"disambiguationData":[OSD([sQuery(id+"F18.wireOp",EDGE,"E11")])],"isStart":false})}),-1.0]])]});
            extrude(context, id + "F23", {"entities" : qUnion([Q0]), "depth" : 6.35 * mm, "offsetDistance" : 25.4 * mm});
        }
        {
            var Q0;
            Q0=makeQuery(id+"F19.opExtrude","SWEPT_BODY",BODY,{"disambiguationData":[OSD([sQuery(id+"F18.wireOp",EDGE,"E11"),sQuery(id+"F18.wireOp",EDGE,"E12")])]});
            var Q1;
            Q1=makeQuery(id+"F21.opExtrude","SWEPT_BODY",BODY,{"disambiguationData":[OSD([sQuery(id+"F20.wireOp",EDGE,"E13.bottom"),sQuery(id+"F20.wireOp",EDGE,"E13.left"),sQuery(id+"F20.wireOp",EDGE,"E13.right"),sQuery(id+"F20.wireOp",EDGE,"E15")])]});
            var Q2;
            Q2=makeQuery(id+"F21.opExtrude","SWEPT_BODY",BODY,{"disambiguationData":[OSD([sQuery(id+"F20.wireOp",EDGE,"E13.top"),sQuery(id+"F20.wireOp",EDGE,"E13.left"),sQuery(id+"F20.wireOp",EDGE,"E13.right"),sQuery(id+"F20.wireOp",EDGE,"E14")])]});
            var Q3;
            Q3=makeQuery(id+"F22.opExtrude","SWEPT_BODY",BODY,{"disambiguationData":[OSD([sQuery(id+"F18.wireOp",EDGE,"E12"),sQuery(id+"F20.wireOp",EDGE,"E13.left"),sQuery(id+"F20.wireOp",EDGE,"E14"),sQuery(id+"F20.wireOp",EDGE,"E15")])]});
            var Q4;
            Q4=makeQuery(id+"F22.opExtrude","SWEPT_BODY",BODY,{"disambiguationData":[OSD([sQuery(id+"F18.wireOp",EDGE,"E12"),sQuery(id+"F20.wireOp",EDGE,"E13.right"),sQuery(id+"F20.wireOp",EDGE,"E14"),sQuery(id+"F20.wireOp",EDGE,"E15")])]});
            var Q5;
            Q5=makeQuery(id+"F23.opExtrude","SWEPT_BODY",BODY,{"disambiguationData":[OSD([sQuery(id+"F18.wireOp",EDGE,"E11"),sQuery(id+"F18.wireOp",EDGE,"E12")])]});
            booleanBodies(context, id + "F24", {"operationType" : BooleanOperationType.UNION, "tools" : qUnion([Q0, Q1, Q2, Q3, Q4, Q5])});
        }
        {
            var Q0;
            Q0=makeQuery(id+"F21.opExtrude","SWEPT_FACE",FACE,{"disambiguationData":[OSD([sQuery(id+"F20.wireOp",EDGE,"E13.top")])]});
            var sketch = newSketch(context, id + "F25", { "sketchPlane" : qUnion([Q0])});
            skCircle(sketch, "E16", {"center": v(52.63, 31.75) * mm, "radius": 3.18 * mm});
            skSolve(sketch);
        }
        {
            var Q0;
            Q0=makeQuery(id+"F25.imprint","IMPRINT",FACE,{"disambiguationData":[TD([[makeQuery(id+"F25.imprint","IMPRINT",EDGE,{"derivedFrom":sQuery(id+"F25.wireOp",EDGE,"E16")}),1.0]])]});
            extrude(context, id + "F26", {"entities" : qUnion([Q0]), "operationType" : NewBodyOperationType.REMOVE, "oppositeDirection" : true, "depth" : 50.8 * mm, "offsetDistance" : 25.4 * mm});
        }
        {
            var Q0;
            Q0=makeQuery(id+"F21.opExtrude","CAP_EDGE",EDGE,{"disambiguationData":[OSD([sQuery(id+"F20.wireOp",EDGE,"E15")])],"isStart":false});
            var Q1;
            Q1=makeQuery(id+"F21.opExtrude","CAP_EDGE",EDGE,{"disambiguationData":[OSD([sQuery(id+"F20.wireOp",EDGE,"E13.bottom")])],"isStart":false});
            var Q2;
            Q2=makeQuery(id+"F21.opExtrude","SWEPT_EDGE",EDGE,{"disambiguationData":[OSD([sQuery(id+"F20.wireOp",EDGE,"E13.bottom"),sQuery(id+"F20.wireOp",EDGE,"E13.right")])]});
            var Q3;
            Q3=makeQuery(id+"F21.opExtrude","SWEPT_EDGE",EDGE,{"disambiguationData":[OSD([sQuery(id+"F20.wireOp",EDGE,"E13.right"),sQuery(id+"F20.wireOp",EDGE,"E15")])]});
            var Q4;
            {var subQ0=sQuery(id+"F20.wireOp",EDGE,"E13.right");Q4=makeQuery(id+"F21.opExtrude","CAP_EDGE",EDGE,{"disambiguationData":[OSD([subQ0]),TDD([makeQuery(id+"F20.imprint","IMPRINT",EDGE,{"disambiguationData":[TD([[makeQuery(id+"F20.imprint","INTERSECT",VERTEX,{"derivedFrom":[sQuery(id+"F20.wireOp",EDGE,"E13.bottom"),subQ0]}),-1.0]])],"derivedFrom":subQ0})])],"isStart":false});}
            var Q5;
            {var subQ0=sQuery(id+"F20.wireOp",EDGE,"E13.left");Q5=makeQuery(id+"F21.opExtrude","CAP_EDGE",EDGE,{"disambiguationData":[OSD([subQ0]),TDD([makeQuery(id+"F20.imprint","IMPRINT",EDGE,{"disambiguationData":[TD([[makeQuery(id+"F20.imprint","INTERSECT",VERTEX,{"derivedFrom":[sQuery(id+"F20.wireOp",EDGE,"E13.bottom"),subQ0]}),-1.0]])],"derivedFrom":subQ0})])],"isStart":false});}
            var Q6;
            Q6=makeQuery(id+"F22.opExtrude","CAP_EDGE",EDGE,{"disambiguationData":[OSD([sQuery(id+"F20.wireOp",EDGE,"E13.right")])],"isStart":false});
            var Q7;
            Q7=makeQuery(id+"F21.opExtrude","SWEPT_EDGE",EDGE,{"disambiguationData":[OSD([sQuery(id+"F20.wireOp",EDGE,"E13.right"),sQuery(id+"F20.wireOp",EDGE,"E14")])]});
            var Q8;
            {var subQ0=sQuery(id+"F20.wireOp",EDGE,"E13.right");Q8=makeQuery(id+"F21.opExtrude","CAP_EDGE",EDGE,{"disambiguationData":[OSD([subQ0]),TDD([makeQuery(id+"F20.imprint","IMPRINT",EDGE,{"disambiguationData":[TD([[makeQuery(id+"F20.imprint","INTERSECT",VERTEX,{"derivedFrom":[sQuery(id+"F20.wireOp",EDGE,"E13.top"),subQ0]}),1.0]])],"derivedFrom":subQ0})])],"isStart":false});}
            var Q9;
            Q9=makeQuery(id+"F21.opExtrude","SWEPT_EDGE",EDGE,{"disambiguationData":[OSD([sQuery(id+"F20.wireOp",EDGE,"E13.top"),sQuery(id+"F20.wireOp",EDGE,"E13.right")])]});
            var Q10;
            Q10=makeQuery(id+"F21.opExtrude","CAP_EDGE",EDGE,{"disambiguationData":[OSD([sQuery(id+"F20.wireOp",EDGE,"E13.top")])],"isStart":false});
            var Q11;
            Q11=makeQuery(id+"F21.opExtrude","SWEPT_EDGE",EDGE,{"disambiguationData":[OSD([sQuery(id+"F20.wireOp",EDGE,"E13.top"),sQuery(id+"F20.wireOp",EDGE,"E13.left")])]});
            var Q12;
            Q12=makeQuery(id+"F21.opExtrude","CAP_EDGE",EDGE,{"disambiguationData":[OSD([sQuery(id+"F20.wireOp",EDGE,"E14")])],"isStart":false});
            var Q13;
            {var subQ0=sQuery(id+"F20.wireOp",EDGE,"E13.left");Q13=makeQuery(id+"F21.opExtrude","CAP_EDGE",EDGE,{"disambiguationData":[OSD([subQ0]),TDD([makeQuery(id+"F20.imprint","IMPRINT",EDGE,{"disambiguationData":[TD([[makeQuery(id+"F20.imprint","INTERSECT",VERTEX,{"derivedFrom":[sQuery(id+"F20.wireOp",EDGE,"E13.top"),subQ0]}),1.0]])],"derivedFrom":subQ0})])],"isStart":false});}
            var Q14;
            Q14=makeQuery(id+"F22.opExtrude","CAP_EDGE",EDGE,{"disambiguationData":[OSD([sQuery(id+"F20.wireOp",EDGE,"E13.left")])],"isStart":false});
            var Q15;
            Q15=makeQuery(id+"F21.opExtrude","SWEPT_EDGE",EDGE,{"disambiguationData":[OSD([sQuery(id+"F20.wireOp",EDGE,"E13.left"),sQuery(id+"F20.wireOp",EDGE,"E15")])]});
            var Q16;
            Q16=makeQuery(id+"F21.opExtrude","SWEPT_EDGE",EDGE,{"disambiguationData":[OSD([sQuery(id+"F20.wireOp",EDGE,"E13.left"),sQuery(id+"F20.wireOp",EDGE,"E14")])]});
            var Q17;
            Q17=makeQuery(id+"F21.opExtrude","SWEPT_EDGE",EDGE,{"disambiguationData":[OSD([sQuery(id+"F20.wireOp",EDGE,"E13.bottom"),sQuery(id+"F20.wireOp",EDGE,"E13.left")])]});
            var Q18;
            {var subQ0=sQuery(id+"F20.wireOp",EDGE,"E13.right");Q18=makeQuery(id+"F24.opBoolean","MERGE",EDGE,{"derivedFrom":[makeQuery(id+"F21.opExtrude","CAP_EDGE",EDGE,{"disambiguationData":[OSD([subQ0]),TDD([makeQuery(id+"F20.imprint","IMPRINT",EDGE,{"disambiguationData":[TD([[makeQuery(id+"F20.imprint","INTERSECT",VERTEX,{"derivedFrom":[sQuery(id+"F20.wireOp",EDGE,"E13.bottom"),subQ0]}),-1.0]])],"derivedFrom":subQ0})])],"isStart":true}),makeQuery(id+"F21.opExtrude","CAP_EDGE",EDGE,{"disambiguationData":[OSD([subQ0]),TDD([makeQuery(id+"F20.imprint","IMPRINT",EDGE,{"disambiguationData":[TD([[makeQuery(id+"F20.imprint","INTERSECT",VERTEX,{"derivedFrom":[sQuery(id+"F20.wireOp",EDGE,"E13.top"),subQ0]}),1.0]])],"derivedFrom":subQ0})])],"isStart":true}),makeQuery(id+"F22.opExtrude","CAP_EDGE",EDGE,{"disambiguationData":[OSD([subQ0])],"isStart":true})]});}
            var Q19;
            Q19=makeQuery(id+"F21.opExtrude","CAP_EDGE",EDGE,{"disambiguationData":[OSD([sQuery(id+"F20.wireOp",EDGE,"E13.bottom")])],"isStart":true});
            var Q20;
            {var subQ0=sQuery(id+"F20.wireOp",EDGE,"E13.left");Q20=makeQuery(id+"F24.opBoolean","MERGE",EDGE,{"derivedFrom":[makeQuery(id+"F21.opExtrude","CAP_EDGE",EDGE,{"disambiguationData":[OSD([subQ0]),TDD([makeQuery(id+"F20.imprint","IMPRINT",EDGE,{"disambiguationData":[TD([[makeQuery(id+"F20.imprint","INTERSECT",VERTEX,{"derivedFrom":[sQuery(id+"F20.wireOp",EDGE,"E13.bottom"),subQ0]}),-1.0]])],"derivedFrom":subQ0})])],"isStart":true}),makeQuery(id+"F21.opExtrude","CAP_EDGE",EDGE,{"disambiguationData":[OSD([subQ0]),TDD([makeQuery(id+"F20.imprint","IMPRINT",EDGE,{"disambiguationData":[TD([[makeQuery(id+"F20.imprint","INTERSECT",VERTEX,{"derivedFrom":[sQuery(id+"F20.wireOp",EDGE,"E13.top"),subQ0]}),1.0]])],"derivedFrom":subQ0})])],"isStart":true}),makeQuery(id+"F22.opExtrude","CAP_EDGE",EDGE,{"disambiguationData":[OSD([subQ0])],"isStart":true})]});}
            var Q21;
            Q21=makeQuery(id+"F21.opExtrude","CAP_EDGE",EDGE,{"disambiguationData":[OSD([sQuery(id+"F20.wireOp",EDGE,"E13.top")])],"isStart":true});
            var Q22;
            Q22=makeQuery(id+"F19.opExtrude","CAP_EDGE",EDGE,{"disambiguationData":[OSD([sQuery(id+"F18.wireOp",EDGE,"E12")])],"isStart":true});
            fillet(context, id + "F27", {"entities" : qUnion([Q0, Q1, Q2, Q3, Q4, Q5, Q6, Q7, Q8, Q9, Q10, Q11, Q12, Q13, Q14, Q15, Q16, Q17, Q18, Q19, Q20, Q21, Q22]), "radius" : 1.27 * mm, "tangentPropagation" : true, "allowEdgeOverflow" : false});
        }
        {
            var Q0;
            Q0=qCreatedBy(makeId("Front.planeOp"),FACE);
            var sketch = newSketch(context, id + "F28", { "sketchPlane" : qUnion([Q0])});
            skCircle(sketch, "E17", {"center": v(25.4, 12.7) * mm, "radius": 3.18 * mm});
            skCircle(sketch, "E18", {"center": v(25.4, 374.65) * mm, "radius": 3.18 * mm});
            skCircle(sketch, "E19", {"center": v(-52.63, 9.52) * mm, "radius": 3.18 * mm});
            skSolve(sketch);
        }
        {
            var Q0;
            Q0 = qSketchRegion(id + "F28", true);
            extrude(context, id + "F29", {"entities" : qUnion([Q0]), "operationType" : NewBodyOperationType.REMOVE, "oppositeDirection" : true, "depth" : 25.4 * mm, "offsetDistance" : 25.4 * mm});
        }
        {
            var Q0;
            Q0=makeQuery(id+"F29.boolean.opBoolean","COPY",FACE,{"derivedFrom":makeQuery(id+"F29.opExtrude","CAP_FACE",FACE,{"disambiguationData":[OSD([sQuery(id+"F28.wireOp",EDGE,"E17")])],"isStart":true})});
            var Q1;
            Q1=makeQuery(id+"F29.boolean.opBoolean","COPY",FACE,{"derivedFrom":makeQuery(id+"F29.opExtrude","CAP_FACE",FACE,{"disambiguationData":[OSD([sQuery(id+"F28.wireOp",EDGE,"E18")])],"isStart":true})});
            extrude(context, id + "F30", {"entities" : qUnion([Q0, Q1]), "operationType" : NewBodyOperationType.REMOVE, "oppositeDirection" : true, "depth" : 25.4 * mm, "offsetDistance" : 25.4 * mm});
        }
        {
            var Q0;
            Q0=makeQuery(id+"F17.opExtrude","CAP_EDGE",EDGE,{"disambiguationData":[OSD([sQuery(id+"F16.wireOp",EDGE,"E10")])],"isStart":false});
            var Q1;
            Q1=makeQuery(id+"F17.opExtrude","CAP_EDGE",EDGE,{"disambiguationData":[OSD([sQuery(id+"F16.wireOp",EDGE,"E10")])],"isStart":true});
            fillet(context, id + "F31", {"entities" : qUnion([Q0, Q1]), "radius" : 1.27 * mm, "tangentPropagation" : true, "allowEdgeOverflow" : false});
        }
        {
            var Q0;
            Q0=makeQuery(id+"F28.imprint","IMPRINT",FACE,{"disambiguationData":[TD([[makeQuery(id+"F28.imprint","IMPRINT",EDGE,{"derivedFrom":sQuery(id+"F28.wireOp",EDGE,"E19")}),1.0]])]});
            extrude(context, id + "F32", {"entities" : qUnion([Q0]), "operationType" : NewBodyOperationType.REMOVE, "oppositeDirection" : true, "depth" : 25.4 * mm, "offsetDistance" : 25.4 * mm});
        }
        {
            var Q0;
            Q0=qCreatedBy(makeId("Top.planeOp"),FACE);
            var sketch = newSketch(context, id + "F33", { "sketchPlane" : qUnion([Q0])});
            skLineSegment(sketch, "E20.bottom", {"start": v(92.1, -1.21) * mm, "end": v(104.8, -1.21) * mm});
            skLineSegment(sketch, "E20.top", {"start": v(92.1, -26.61) * mm, "end": v(104.8, -26.61) * mm});
            skLineSegment(sketch, "E20.left", {"start": v(92.1, -1.21) * mm, "end": v(92.1, -26.61) * mm});
            skLineSegment(sketch, "E20.right", {"start": v(104.8, -1.21) * mm, "end": v(104.8, -26.61) * mm});
            skLineSegment(sketch, "E21.bottom", {"start": v(110.65, -39.31) * mm, "end": v(85.25, -39.31) * mm});
            skLineSegment(sketch, "E21.top", {"start": v(110.65, 11.49) * mm, "end": v(85.25, 11.49) * mm});
            skLineSegment(sketch, "E21.left", {"start": v(110.65, -39.31) * mm, "end": v(110.65, 11.49) * mm});
            skLineSegment(sketch, "E21.right", {"start": v(85.25, -39.31) * mm, "end": v(85.25, 11.49) * mm});
            skPoint(sketch, "E21.middle", {"position": v(97.95, -13.91) * mm});
            skPoint(sketch, "E21.middle.positionSnap0", {"position": v(92.1, -13.91) * mm});
            skPoint(sketch, "E21.centerSnap0", {"position": v(92.1, -13.91) * mm});
            skCircle(sketch, "E22", {"center": v(97.95, 5.14) * mm, "radius": 3.18 * mm});
            skCircle(sketch, "E23", {"center": v(97.95, -32.96) * mm, "radius": 3.18 * mm});
            skSolve(sketch);
        }
        {
            var Q0;
            Q0=makeQuery(id+"F33.imprint","IMPRINT",FACE,{"disambiguationData":[TD([[makeQuery(id+"F33.imprint","IMPRINT",EDGE,{"derivedFrom":sQuery(id+"F33.wireOp",EDGE,"E20.bottom")}),1.0]])]});
            extrude(context, id + "F34", {"entities" : qUnion([Q0]), "depth" : 6.35 * mm, "offsetDistance" : 25.4 * mm});
        }
        {
            var Q0;
            Q0=makeQuery(id+"F33.imprint","IMPRINT",FACE,{"disambiguationData":[TD([[makeQuery(id+"F33.imprint","IMPRINT",EDGE,{"derivedFrom":sQuery(id+"F33.wireOp",EDGE,"E20.bottom")}),-1.0]])]});
            extrude(context, id + "F35", {"entities" : qUnion([Q0]), "operationType" : NewBodyOperationType.ADD, "depth" : 44.45 * mm, "offsetDistance" : 25.4 * mm});
        }
        {
            var Q0;
            Q0=makeQuery(id+"F35.opExtrude","CAP_EDGE",EDGE,{"disambiguationData":[OSD([sQuery(id+"F33.wireOp",EDGE,"E20.top")])],"isStart":false});
            var Q1;
            Q1=makeQuery(id+"F35.opExtrude","CAP_EDGE",EDGE,{"disambiguationData":[OSD([sQuery(id+"F33.wireOp",EDGE,"E20.bottom")])],"isStart":false});
            fillet(context, id + "F36", {"entities" : qUnion([Q0, Q1]), "radius" : 12.7 * mm, "tangentPropagation" : true, "allowEdgeOverflow" : false});
        }
        {
            var Q0;
            Q0=makeQuery(id+"F35.opExtrude","SWEPT_FACE",FACE,{"disambiguationData":[OSD([sQuery(id+"F33.wireOp",EDGE,"E20.right")])]});
            var sketch = newSketch(context, id + "F37", { "sketchPlane" : qUnion([Q0])});
            skCircle(sketch, "E24", {"center": v(-13.91, 31.75) * mm, "radius": 3.17 * mm});
            skSolve(sketch);
        }
        {
            var Q0;
            Q0=makeQuery(id+"F37.imprint","IMPRINT",FACE,{"disambiguationData":[TD([[makeQuery(id+"F37.imprint","IMPRINT",EDGE,{"derivedFrom":sQuery(id+"F37.wireOp",EDGE,"E24")}),1.0]])]});
            extrude(context, id + "F38", {"entities" : qUnion([Q0]), "operationType" : NewBodyOperationType.REMOVE, "oppositeDirection" : true, "depth" : 25.4 * mm, "offsetDistance" : 25.4 * mm});
        }
        {
            var Q0;
            Q0=makeQuery(id+"F17.opExtrude","CAP_FACE",FACE,{"disambiguationData":[OSD([sQuery(id+"F16.wireOp",EDGE,"E10")])],"isStart":false});
            var sketch = newSketch(context, id + "F39", { "sketchPlane" : qUnion([Q0])});
            skCircle(sketch, "E25", {"center": v(25.4, 0) * mm, "radius": 4.13 * mm});
            skSolve(sketch);
        }
        {
            var Q0;
            Q0=makeQuery(id+"F39.imprint","IMPRINT",FACE,{"disambiguationData":[TD([[makeQuery(id+"F39.imprint","IMPRINT",EDGE,{"derivedFrom":sQuery(id+"F39.wireOp",EDGE,"E25")}),1.0]])]});
            extrude(context, id + "F40", {"entities" : qUnion([Q0]), "operationType" : NewBodyOperationType.REMOVE, "oppositeDirection" : true, "depth" : 508 * mm, "offsetDistance" : 25.4 * mm});
        }
        {
            var Q0;
            Q0=makeQuery(id+"F9.opExtrude","SWEPT_FACE",FACE,{"disambiguationData":[OSD([sQuery(id+"F4.wireOp",EDGE,"E6.bottom"),sQuery(id+"F4.wireOp",EDGE,"E6.top"),sQuery(id+"F4.wireOp",EDGE,"E6.right")])]});
            var sketch = newSketch(context, id + "F41", { "sketchPlane" : qUnion([Q0])});
            skCircle(sketch, "E26", {"center": v(26.67, 166.37) * mm, "radius": 6.35 * mm});
            skSolve(sketch);
        }
        {
            var Q0;
            Q0 = qSketchRegion(id + "F41", true);
            extrude(context, id + "F42", {"entities" : qUnion([Q0]), "depth" : 33.02 * mm, "offsetDistance" : 25.4 * mm});
        }
        {
            var Q0;
            Q0=makeQuery(id+"F9.opExtrude","SWEPT_FACE",FACE,{"disambiguationData":[OSD([sQuery(id+"F4.wireOp",EDGE,"E6.bottom"),sQuery(id+"F4.wireOp",EDGE,"E6.left"),sQuery(id+"F4.wireOp",EDGE,"E6.right")])]});
            cPlane(context, id + "F43", {"entities" : qUnion([Q0]), "cplaneType" : CPlaneType.OFFSET, "offset" : 0 * mm, "width" : 152.4 * mm, "height" : 152.4 * mm});
        }
        {
            var Q0;
            Q0=qCreatedBy(id+"F43.planeOp",FACE);
            var sketch = newSketch(context, id + "F44", { "sketchPlane" : qUnion([Q0])});
            skCircle(sketch, "E27", {"center": v(-33.02, 166.37) * mm, "radius": 1.59 * mm});
            skSolve(sketch);
        }
        {
            var Q0;
            Q0=makeQuery(id+"F44.imprint","IMPRINT",FACE,{"disambiguationData":[TD([[makeQuery(id+"F44.imprint","IMPRINT",EDGE,{"derivedFrom":sQuery(id+"F44.wireOp",EDGE,"E27")}),1.0]])]});
            extrude(context, id + "F45", {"entities" : qUnion([Q0]), "operationType" : NewBodyOperationType.REMOVE, "oppositeDirection" : true, "depth" : 25.4 * mm, "offsetDistance" : 25.4 * mm});
        }
        {
            var Q0;
            Q0=makeQuery(id+"F42.opExtrude","CAP_EDGE",EDGE,{"disambiguationData":[OSD([sQuery(id+"F41.wireOp",EDGE,"E26")])],"isStart":false});
            fillet(context, id + "F46", {"entities" : qUnion([Q0]), "radius" : 3.17 * mm, "tangentPropagation" : true, "allowEdgeOverflow" : false});
        }
    });
